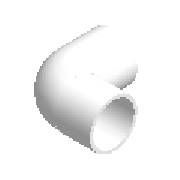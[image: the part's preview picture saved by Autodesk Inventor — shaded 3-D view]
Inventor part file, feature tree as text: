
AUTODESK INVENTOR PART (.ipt)
format: ipt  version: 2023 (Build 270158000, 158)  size: 224,256 bytes
history: native  units: mm (DEFAULTED — no unit token found)
features: other x6, revolve x3, sketch x2, projected_geometry x1
ambient origin geometry x8: Origin, YZ Plane, XZ Plane, XY Plane, X Axis, Y Axis, Z Axis, Center Point
bodies: Solid1 (feature_tree)
feature tree (12):
  sketch  "Sketch1"  dims[d0=61.0mm d1=56.0mm]
  revolve  "Revolution1"  [1 undecoded]
  revolve  "Revolution2"  [1 undecoded]
  revolve  "Revolution3"  [1 undecoded]
  other  "Work Axis1"
  other  "Work Point1"
  other  "Work Point2"
  other  "Work Axis2"
  other  "Work Point3"
  other  "Work Point4"
  sketch  "Sketch2"  dims[d2=110.0mm d3=8.2mm d4=61.0mm d5=8.2mm d6=110.0mm d7=56.0mm d139=90.0deg d140=90.0deg d8=0.01mm d9=126.4mm d10=104.5mm d11=90.0deg]
  projected_geometry  "Projected Loop2"
note: 3 required parameter values undecoded (feature->parameter linkage not recoverable at this tier; creation-order binding heuristic only, values carry confidence <= 0.55)
